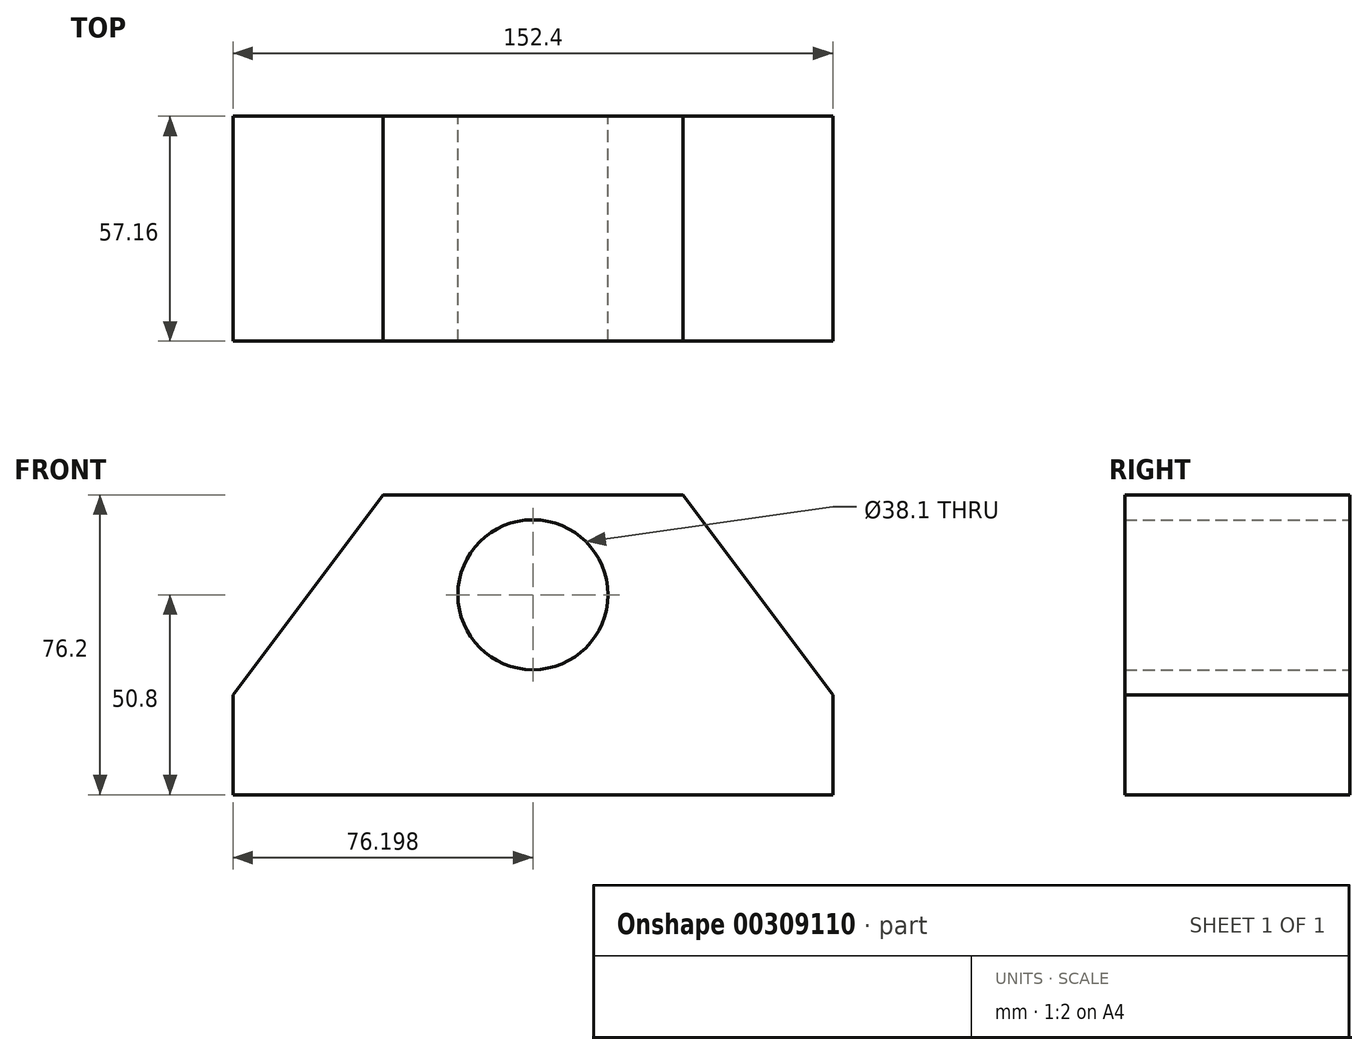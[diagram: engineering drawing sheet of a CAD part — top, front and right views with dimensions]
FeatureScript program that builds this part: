
annotation { "Feature Type Name" : "Feature", "Feature Type Description" : "" }
export const myFeature = defineFeature(function(context is Context, id is Id, definition is map)
    precondition{}
    {
        {
            var Q0;
            Q0=qCreatedBy(makeId("Front.planeOp"),FACE);
            var sketch = newSketch(context, id + "F0", { "sketchPlane" : qUnion([Q0])});
            skLineSegment(sketch, "E0", {"start": v(-68.78, 0) * mm, "end": v(83.62, 0) * mm});
            skLineSegment(sketch, "E1", {"start": v(83.62, 0) * mm, "end": v(83.62, 25.4) * mm});
            skLineSegment(sketch, "E2", {"start": v(83.62, 25.4) * mm, "end": v(45.52, 76.2) * mm});
            skLineSegment(sketch, "E3", {"start": v(45.52, 76.2) * mm, "end": v(-30.68, 76.2) * mm});
            skLineSegment(sketch, "E4", {"start": v(-30.68, 76.2) * mm, "end": v(-68.78, 25.4) * mm});
            skLineSegment(sketch, "E5", {"start": v(-68.78, 25.4) * mm, "end": v(-68.78, 0) * mm});
            skCircle(sketch, "E6", {"center": v(7.42, 50.8) * mm, "radius": 19.05 * mm});
            skSolve(sketch);
        }
        {
            var Q0;
            Q0=makeQuery(id+"F0.imprint","IMPRINT",FACE,{"disambiguationData":[TD([[makeQuery(id+"F0.imprint","IMPRINT",EDGE,{"derivedFrom":sQuery(id+"F0.wireOp",EDGE,"E0")}),1.0]])]});
            extrude(context, id + "F1", {"entities" : qUnion([Q0]), "depth" : 57.15 * mm, "symmetric" : true});
        }
    });
